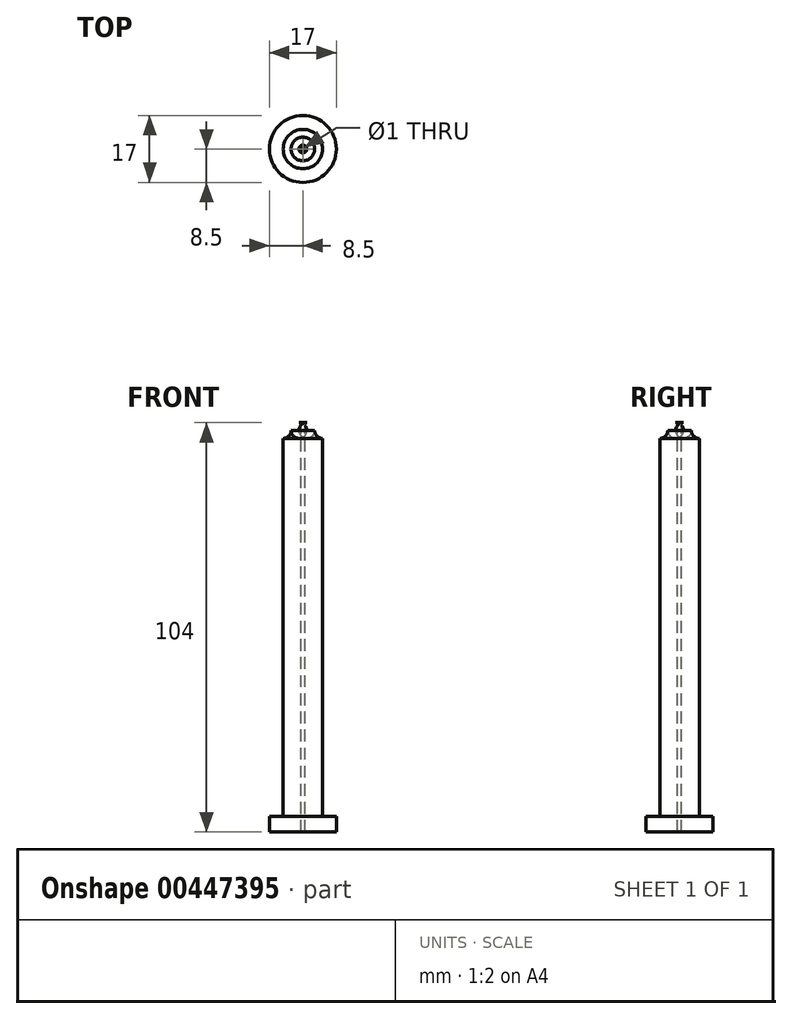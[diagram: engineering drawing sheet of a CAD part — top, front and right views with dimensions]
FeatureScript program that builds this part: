
annotation { "Feature Type Name" : "Feature", "Feature Type Description" : "" }
export const myFeature = defineFeature(function(context is Context, id is Id, definition is map)
    precondition{}
    {
        {
            var Q0;
            Q0=qCreatedBy(makeId("Top.planeOp"),FACE);
            var sketch = newSketch(context, id + "F0", { "sketchPlane" : qUnion([Q0])});
            skCircle(sketch, "E0", {"center": v(0, 0) * mm, "radius": 8.5 * mm});
            skSolve(sketch);
        }
        {
            var Q0;
            Q0=qSketchRegion(id+"F0",true);
            extrude(context, id + "F1", {"entities" : qUnion([Q0]), "depth" : 4 * mm});
        }
        {
            var Q0;
            Q0=qCreatedBy(makeId("Top.planeOp"),FACE);
            var sketch = newSketch(context, id + "F2", { "sketchPlane" : qUnion([Q0])});
            skCircle(sketch, "E1", {"center": v(0, 0) * mm, "radius": 5 * mm});
            skSolve(sketch);
        }
        {
            var Q0;
            Q0=qSketchRegion(id+"F2",true);
            extrude(context, id + "F3", {"entities" : qUnion([Q0]), "operationType" : NewBodyOperationType.ADD, "depth" : 100 * mm});
        }
        {
            var Q0;
            Q0=qCreatedBy(makeId("Right.planeOp"),FACE);
            var sketch = newSketch(context, id + "F4", { "sketchPlane" : qUnion([Q0])});
            skLineSegment(sketch, "E2", {"start": v(0, 102) * mm, "end": v(0, 100) * mm});
            skLineSegment(sketch, "E3", {"start": v(0, 100) * mm, "end": v(5, 100) * mm});
            skLineSegment(sketch, "E4", {"start": v(3, 102) * mm, "end": v(0, 102) * mm});
            skArc(sketch, "E5", {"start": v(3, 102) * mm, "mid": v(3.59, 100.59) * mm, "end": v(5, 100) * mm});
            skSolve(sketch);
        }
        {
            var Q0;
            Q0=makeQuery(id+"F4.imprint","IMPRINT",FACE,{"disambiguationData":[TD([[makeQuery(id+"F4.imprint","IMPRINT",EDGE,{"derivedFrom":sQuery(id+"F4.wireOp",EDGE,"E2")}),1.0]])]});
            var Q1;
            Q1=sQuery(id+"F4.wireOp",EDGE,"E2");
            revolve(context, id + "F5", {"operationType" : NewBodyOperationType.ADD, "entities" : qUnion([Q0]), "axis" : qUnion([Q1]), "revolveType" : RevolveType.FULL});
        }
        {
            var Q0;
            Q0=qCreatedBy(makeId("Right.planeOp"),FACE);
            var sketch = newSketch(context, id + "F6", { "sketchPlane" : qUnion([Q0])});
            skLineSegment(sketch, "E6", {"start": v(0, 102) * mm, "end": v(0, 104) * mm});
            skLineSegment(sketch, "E7", {"start": v(0, 104) * mm, "end": v(1, 104) * mm});
            skLineSegment(sketch, "E8", {"start": v(3, 102) * mm, "end": v(0, 102) * mm});
            skArc(sketch, "E9", {"start": v(3, 102) * mm, "mid": v(2.41, 103.41) * mm, "end": v(1, 104) * mm});
            skSolve(sketch);
        }
        {
            var Q0;
            Q0=makeQuery(id+"F6.imprint","IMPRINT",FACE,{"disambiguationData":[TD([[makeQuery(id+"F6.imprint","IMPRINT",EDGE,{"derivedFrom":sQuery(id+"F6.wireOp",EDGE,"E6")}),-1.0]])]});
            var Q1;
            Q1=sQuery(id+"F6.wireOp",EDGE,"E6");
            revolve(context, id + "F7", {"operationType" : NewBodyOperationType.ADD, "entities" : qUnion([Q0]), "axis" : qUnion([Q1]), "revolveType" : RevolveType.FULL});
        }
        {
            var Q0;
            Q0=makeQuery(id+"F7.opRevolve","SWEPT_FACE",FACE,{"disambiguationData":[OSD([sQuery(id+"F6.wireOp",EDGE,"E7")])]});
            var sketch = newSketch(context, id + "F8", { "sketchPlane" : qUnion([Q0])});
            skCircle(sketch, "E10", {"center": v(0, 0) * mm, "radius": 0.5 * mm});
            skSolve(sketch);
        }
        {
            var Q0;
            Q0 = qSketchRegion(id + "F8", true);
            extrude(context, id + "F9", {"entities" : qUnion([Q0]), "operationType" : NewBodyOperationType.REMOVE, "oppositeDirection" : true, "depth" : 114.1 * mm});
        }
    });
